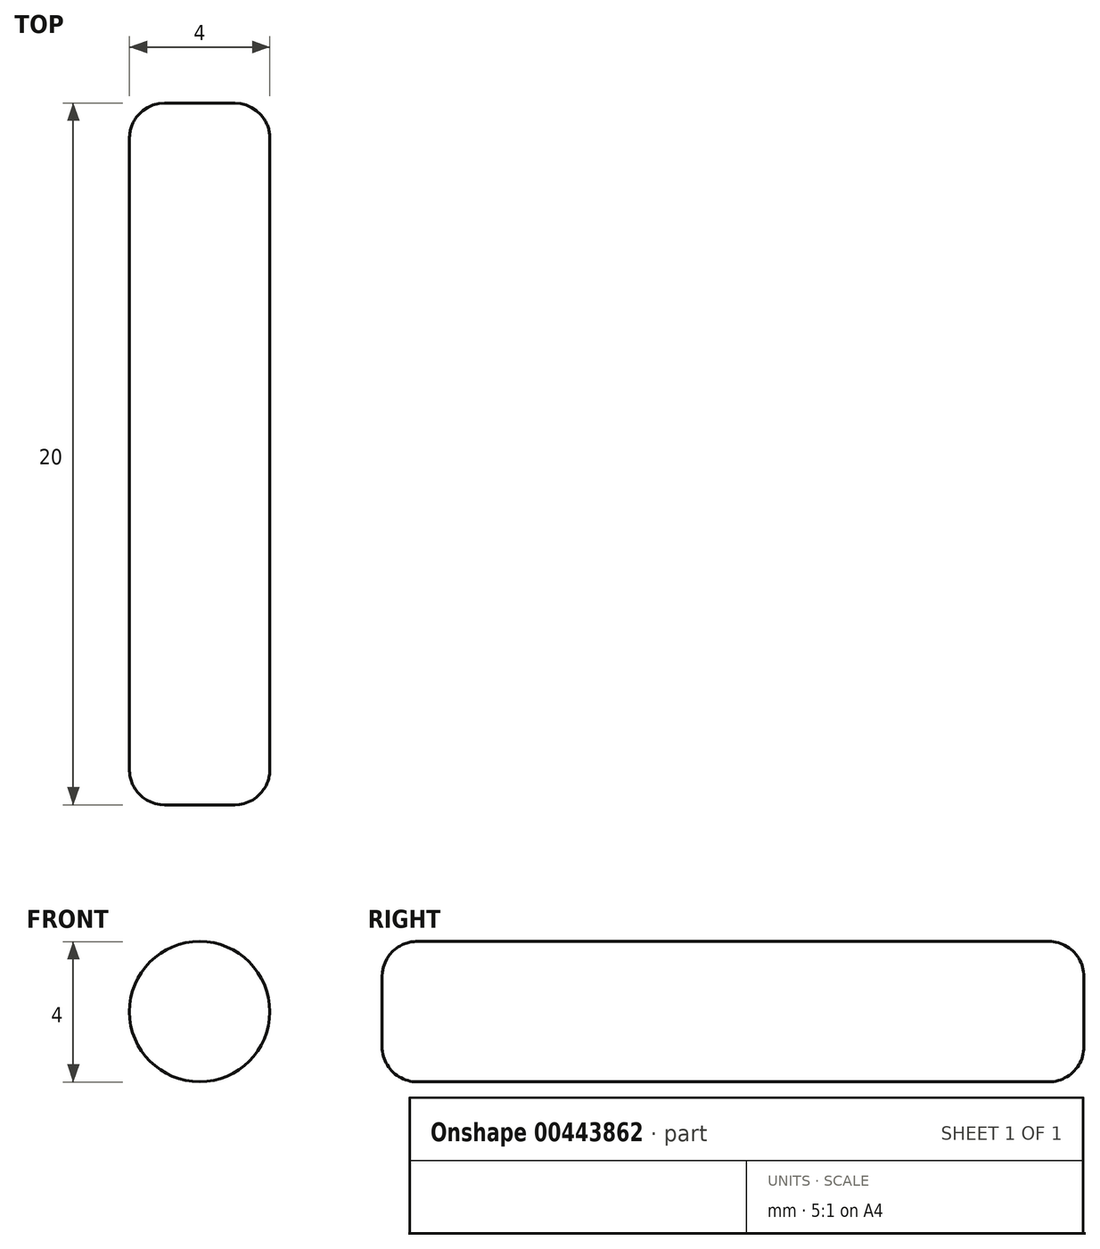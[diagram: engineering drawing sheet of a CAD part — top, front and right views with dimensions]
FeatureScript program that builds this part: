
annotation { "Feature Type Name" : "Feature", "Feature Type Description" : "" }
export const myFeature = defineFeature(function(context is Context, id is Id, definition is map)
    precondition{}
    {
        {
            var Q0;
            Q0=qCreatedBy(makeId("Front.planeOp"),FACE);
            var sketch = newSketch(context, id + "F0", { "sketchPlane" : qUnion([Q0])});
            skCircle(sketch, "E0", {"center": v(0, 0.05) * mm, "radius": 2 * mm});
            skSolve(sketch);
        }
        {
            var Q0;
            Q0 = qSketchRegion(id + "F0", true);
            extrude(context, id + "F1", {"entities" : qUnion([Q0]), "endBound" : BoundingType.SYMMETRIC, "depth" : 20 * mm});
        }
        {
            var Q0;
            Q0=makeQuery(id+"F0.imprint","IMPRINT",FACE,{"disambiguationData":[TD([[makeQuery(id+"F0.imprint","IMPRINT",EDGE,{"derivedFrom":sQuery(id+"F0.wireOp",EDGE,"E0")}),1.0]])]});
            extrude(context, id + "F2", {"entities" : qUnion([Q0]), "operationType" : NewBodyOperationType.ADD, "endBound" : BoundingType.SYMMETRIC, "depth" : 20 * mm});
        }
        {
            var Q0;
            Q0=makeQuery(id+"F1.opExtrude","CAP_FACE",FACE,{"disambiguationData":[OSD([sQuery(id+"F0.wireOp",EDGE,"E0")])],"isStart":false});
            var Q1;
            Q1=makeQuery(id+"F1.opExtrude","CAP_EDGE",EDGE,{"disambiguationData":[OSD([sQuery(id+"F0.wireOp",EDGE,"E0")])],"isStart":false});
            var Q2;
            Q2=makeQuery(id+"F1.opExtrude","CAP_FACE",FACE,{"disambiguationData":[OSD([sQuery(id+"F0.wireOp",EDGE,"E0")])],"isStart":true});
            var Q3;
            Q3=makeQuery(id+"F1.opExtrude","CAP_EDGE",EDGE,{"disambiguationData":[OSD([sQuery(id+"F0.wireOp",EDGE,"E0")])],"isStart":true});
            fillet(context, id + "F3", {"entities" : qUnion([Q0, Q1, Q2, Q3]), "radius" : 1 * mm, "tangentPropagation" : true, "allowEdgeOverflow" : false});
        }
    });
